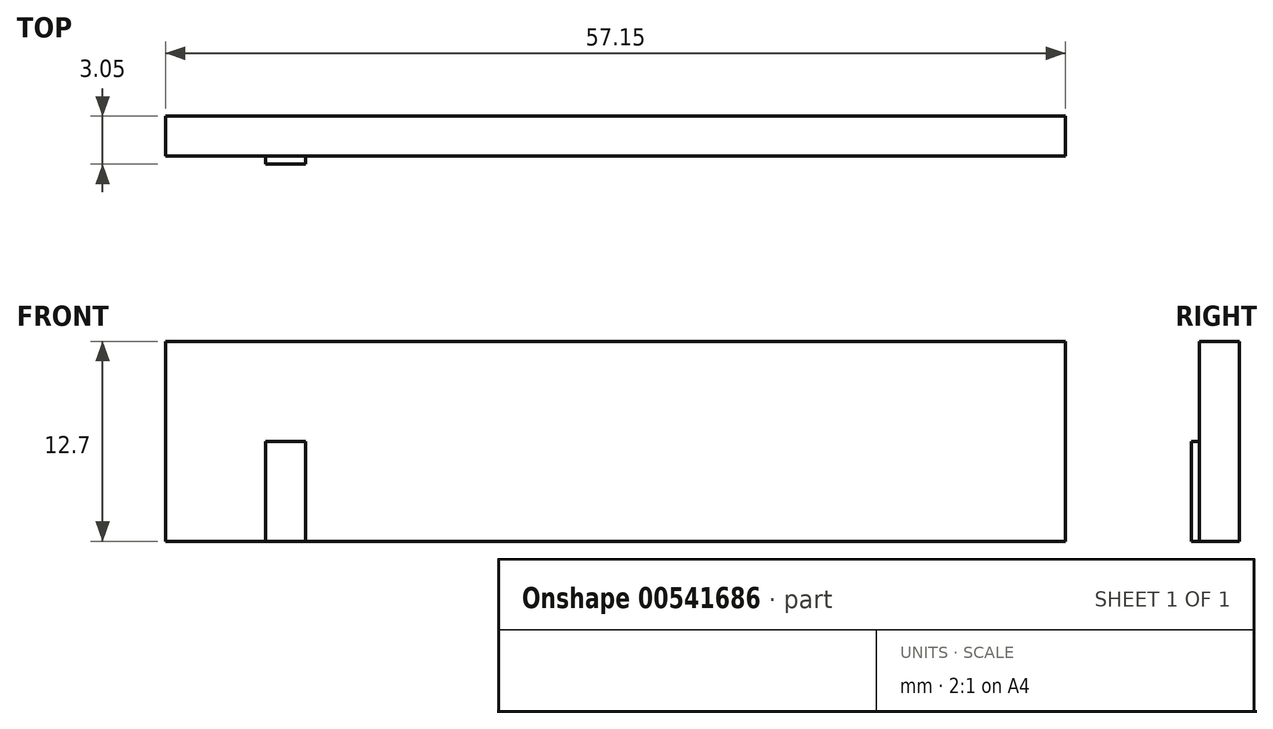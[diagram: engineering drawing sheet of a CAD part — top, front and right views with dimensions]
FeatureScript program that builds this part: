
annotation { "Feature Type Name" : "Feature", "Feature Type Description" : "" }
export const myFeature = defineFeature(function(context is Context, id is Id, definition is map)
    precondition{}
    {
        {
            var Q0;
            Q0=qCreatedBy(makeId("Top.planeOp"),FACE);
            var sketch = newSketch(context, id + "F0", { "sketchPlane" : qUnion([Q0])});
            skLineSegment(sketch, "E0.bottom", {"start": v(-31.9, -4.74) * mm, "end": v(-34.45, -4.74) * mm});
            skLineSegment(sketch, "E0.left", {"start": v(-31.9, -4.74) * mm, "end": v(-31.9, -4.23) * mm});
            skLineSegment(sketch, "E0.right", {"start": v(-34.45, -4.74) * mm, "end": v(-34.45, -4.23) * mm});
            skPoint(sketch, "E0.middle", {"position": v(-33.18, -4.49) * mm});
            skLineSegment(sketch, "E1.bottom", {"start": v(16.35, -4.23) * mm, "end": v(-31.9, -4.23) * mm});
            skLineSegment(sketch, "E1.top", {"start": v(16.35, -1.7) * mm, "end": v(-40.8, -1.7) * mm});
            skLineSegment(sketch, "E1.left", {"start": v(16.35, -4.23) * mm, "end": v(16.35, -1.7) * mm});
            skLineSegment(sketch, "E1.right", {"start": v(-40.8, -4.23) * mm, "end": v(-40.8, -1.7) * mm});
            skPoint(sketch, "E1.middle", {"position": v(-12.22, -2.96) * mm});
            skLineSegment(sketch, "E2.trimOffspring", {"start": v(-34.45, -4.23) * mm, "end": v(-40.8, -4.23) * mm});
            skSolve(sketch);
        }
        {
            var Q0;
            Q0 = qSketchRegion(id + "F0", true);
            extrude(context, id + "F1", {"entities" : qUnion([Q0]), "depth" : 6.35 * mm, "offsetDistance" : 25.4 * mm});
        }
        {
            var Q0;
            Q0=makeQuery(id+"F1.opExtrude","CAP_FACE",FACE,{"disambiguationData":[OSD([sQuery(id+"F0.wireOp",EDGE,"E0.bottom"),sQuery(id+"F0.wireOp",EDGE,"E0.left"),sQuery(id+"F0.wireOp",EDGE,"E0.right"),sQuery(id+"F0.wireOp",EDGE,"E1.bottom"),sQuery(id+"F0.wireOp",EDGE,"E1.top"),sQuery(id+"F0.wireOp",EDGE,"E1.left"),sQuery(id+"F0.wireOp",EDGE,"E1.right"),sQuery(id+"F0.wireOp",EDGE,"E2.trimOffspring")])],"isStart":false});
            var sketch = newSketch(context, id + "F2", { "sketchPlane" : qUnion([Q0])});
            skLineSegment(sketch, "E3.bottom", {"start": v(16.35, -1.7) * mm, "end": v(-40.8, -1.7) * mm});
            skLineSegment(sketch, "E3.top", {"start": v(16.35, -4.23) * mm, "end": v(-40.8, -4.23) * mm});
            skLineSegment(sketch, "E3.left", {"start": v(16.35, -1.7) * mm, "end": v(16.35, -4.23) * mm});
            skLineSegment(sketch, "E3.right", {"start": v(-40.8, -1.7) * mm, "end": v(-40.8, -4.23) * mm});
            skPoint(sketch, "E3.middle", {"position": v(-12.22, -2.96) * mm});
            skPoint(sketch, "E3.middle.positionSnap0", {"position": v(16.35, -2.96) * mm});
            skPoint(sketch, "E3.middle.positionSnap1", {"position": v(-12.22, -1.7) * mm});
            skPoint(sketch, "E3.centerSnap0", {"position": v(16.35, -2.96) * mm});
            skPoint(sketch, "E3.centerSnap1", {"position": v(-12.22, -1.7) * mm});
            skSolve(sketch);
        }
        {
            var Q0;
            Q0 = qSketchRegion(id + "F2", true);
            extrude(context, id + "F3", {"entities" : qUnion([Q0]), "operationType" : NewBodyOperationType.ADD, "depth" : 6.35 * mm, "offsetDistance" : 25.4 * mm});
        }
    });
